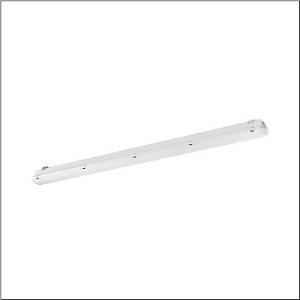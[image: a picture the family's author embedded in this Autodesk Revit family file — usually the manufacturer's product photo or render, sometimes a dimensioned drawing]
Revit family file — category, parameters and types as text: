
# Revit family: monsun_r__11xtreme_ho_51fe10dp480s_3f43
name_source: partatom
category: Lighting Fixtures
units: mm (PartAtom-declared; Revit-internal decimal feet)

## family parameters
Cut with Voids When Loaded = No
Host = Face
Light Source = No
Part Type = Normal
Room Calculation Point = No
Round Connector Dimension = Use Diameter
Shared = No

## types (1)
- --- (1 x LED, 8000 lm, 41 W, 4000K)
    Apparent Load = 41 VA
    CIE Flux Codes = 47 76 93 94 100
    Color Rendering = 80
    Color Temperature = 4000K
    Default Elevation = 1800 mm
    Description = Monsun® 11Xtreme HO, damp-proof luminaire, chain hanger, primary optical cover: enclosure, of PMMA, light emission: direct distribution, primary light characteristic: symmetric, installation type: suspended mounting, surface-mounted, horizontal mounting, vertical mounting, LED, rated luminous flux: 8.000lm, luminous efficacy: 195lm/W, light colour: 840, colour temperature: 4000K, control gear: DALI 2, with terminal, 5-pole, max. 2.5mm², mains connection: 220..240V, AC, 50/60Hz, rated input power: 41W, luminaire housing, of glass-fibre reinforced polyester, uncoated, bright grey, incl. chain hanger, length: 1.590mm, width: 90mm, height: 88mm, clip for enclosure, of stainless steel (V2A), ceiling mounting element, of stainless steel (V2A), chain hanger, of stainless steel (V2A), protection rating (complete): IP66, insulation class (complete): insulation class I (protective earthing), certification: CE, ENEC, VDE, UKCA, protection symbol: D, impact resistance: IK04, permissible operating ambient temperature: -35..+55°C, standard: EN 50419, EN 60598-2-1, contact your sales advisor before using the luminaires in applications with unclear chemical exposure, large temperature fluctuations or condensation-forming humidity, LABS conformity tested according to VDMA 24364:2018-05, no direct snow, no direct sun, no direct rain, for indoor or canopied outdoor use, corresponds to IFS (International Featured Standards) requirements for safety and quality in the food industry, packaging unit: 1 piece
    Height = 88 mm
    Lamp = 1 x LED
    Lamp Light Flux = 8000 lm
    Lamp Power = 41 W
    Lamp count = 1
    Length = 1590 mm
    Luminous efficacy = 195 lm/W
    Manufacturer = Siteco
    ModVariant = No
    Model = 51FE10DP480S
    Mounting Place = Ceiling
    Mounting Type = Surface mounted
    Number of Poles = 1
    OnlyDefault = Yes
    Power Factor = 1
    Product Name = Monsun® 11Xtreme HO
    Product group = damp-proof luminaire
    ProductGroupID = 300
    Protection Class = Protection class I
    Protection Degree = IP 66
    RLX_Detail_Level = 1
    RLX_Emergency_Light_Flux = 0 lm
    RLX_Emergency_Type = 0
    RLX_Emergency_Type_DB = No
    RlxData = <blob elided: 87061 chars, md5=13d3e86c>
    Socket = socket
    Standby Power = 0 W
    System Light Flux = 8000 lm
    System Power = 41 W
    Type Comments = factory setting: luminous flux: 100 % | dim-lin: 254 | 284 mA
    Type Image = l_1349234.jpg
    URL = http://relux.com
    VarID = @adj_023076
    Voltage = 0 V
    Weight = 0.00 kg
    Width = 90 mm

## geometry (parser evidence)
native form markers: Blend x4, Sweep x12
no freeform markers — native parametric forms only
